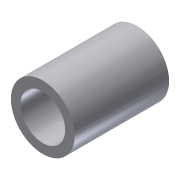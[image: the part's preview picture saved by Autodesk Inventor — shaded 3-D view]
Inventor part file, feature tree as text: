
AUTODESK INVENTOR PART (.ipt)
format: ipt  version: 2013 (Build 170138000, 138)  size: 83,968 bytes
history: native  units: in
note: dims shown in document units (in); Inventor stores cm internally (conversion verified against a paired STEP export)
features: extrude x1, sketch x1
ambient origin geometry x8: Origin, YZ Plane, XZ Plane, XY Plane, X Axis, Y Axis, Z Axis, Center Point
bodies: Solid1 (feature_tree)
feature tree (2):
  extrude  "Extrusion1"  Depth=0.675in
  sketch  "Sketch1"  dims[d0=0.473in d2=0.675in d4=0.0in]
